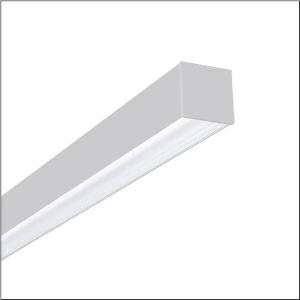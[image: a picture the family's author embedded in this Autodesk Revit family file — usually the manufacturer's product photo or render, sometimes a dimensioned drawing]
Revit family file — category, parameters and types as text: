
# Revit family: silica_r_5mx22wd1w4a_c31c
name_source: partatom
category: Lighting Fixtures
units: mm (PartAtom-declared; Revit-internal decimal feet)

## family parameters
Cut with Voids When Loaded = No
Host = Face
Light Source = No
Part Type = Normal
Room Calculation Point = No
Round Connector Dimension = Use Diameter
Shared = No

## types (1)
- --- (1 x LED, 4680 lm, 29.3 W, 4000K)
    Apparent Load = 29 VA
    CIE Flux Codes = 70 95 99 100 100
    Color Rendering = 80
    Color Temperature = 4000K
    Default Elevation = 1800 mm
    Description = Silica®, office luminaire, primary light control with wallwasher, of aluminium, light emission: direct distribution, primary light characteristic: asymmetric, installation type: surface-mounted, LED, rated luminous flux: 4.680lm, luminous efficacy: 160lm/W, light colour: 840, colour temperature: 4000K, control gear: ECG DALI, with terminal, 3+2-pole, max. 2.5mm², mains connection: 230V, AC, 50/60Hz, rated input power: 29W, luminaire housing, of aluminium, traffic white (RAL 9016), length: 1.442mm, width: 65mm, height: 64mm, protection rating (complete): IP20, insulation class (complete): insulation class I (protective earthing), certification: CE, permissible operating ambient temperature: 0..+35°C, standard: EN 50419, packaging unit: 1 piece
    Height = 64 mm
    Lamp = 1 x LED
    Lamp Light Flux = 4680 lm
    Lamp Power = 29.3 W
    Lamp count = 1
    Length = 1442 mm
    Luminous efficacy = 160 lm/W
    Manufacturer = Siteco
    ModVariant = No
    Model = 5MX22WD1W4A
    Mounting Place = Ceiling
    Mounting Type = Surface mounted
    Number of Poles = 1
    OnlyDefault = Yes
    Power Factor = 1
    Product Name = Silica®
    Product group = office luminaire | ceiling mounted
    ProductGroupID = 304
    Protection Class = Protection class I
    Protection Degree = IP 20
    RLX_Detail_Level = 1
    RLX_Emergency_Light_Flux = 0 lm
    RLX_Emergency_Type = 0
    RLX_Emergency_Type_DB = No
    RlxData = <blob elided: 23949 chars, md5=1a20c4a7>
    Socket = socket
    Standby Power = 0 W
    System Light Flux = 4680 lm
    System Power = 29 W
    Type Comments = factory setting: luminous flux: 100 % | dim-lin: 254 | 164 mA
    Type Image = l_1003937.jpg
    URL = http://relux.com
    VarID = @adj_138302
    Voltage = 0 V
    Weight = 0.00 kg
    Width = 66 mm

## geometry (parser evidence)
native form markers: Blend x4, Sweep x10
no freeform markers — native parametric forms only
